# Revit family: Sink-Lavatory-KOHLER-Odeon-K-11160
name_source: partatom
category: Plumbing Fixtures
revit_build: Autodesk Revit 2015 (Build: 20140606_1530(x64)
units: mm (PartAtom-declared; Revit-internal decimal feet)

## types (2) — shared parameters
ADA Compliant = No
Assembly Code = D2010400
CW Connection = No
Cold Water Inlet = Cold Water Inlet
Date Modified = 09/25/2018
Default Elevation = 36"
Drain Included = No
Finish = Kohler-Vitreous_China-0-White
HW Connection = No
Height = 8"
Hot Water Inlet = Hot Water Inlet
Length = 22"
Manufacturer = KOHLER Co.
MasterFormat 1995 = 15410
MasterFormat 2004 = 22.41.16
Material = Vitreous China
Product Documentation Link = http://www.us.kohler.com
Product Name = Odeon
Product Page URL = http://www.us.kohler.com
URL = https://www.us.kohler.com
Vent Connection = No
Waste Connection = Yes
Waste Water Outlet = Waste Water Outlet
Width = 17 7/8"

## per-type parameters (varying)
| type | Description | Model | Single Faucet Hole | Three Faucet Holes | Type |
| Single Faucet Hole, 0 - White | Drop-in bathroom sink with single faucet hole | K-11160-1-0 | Yes | No | 1 |
| Three Faucet Holes, 0 - White | Drop-in bathroom sink with 4 inch centerset faucet holes | K-11160-4-0 | No | Yes | 2 |

## geometry (parser evidence)
native form markers: Sweep x8
no freeform markers — native parametric forms only
